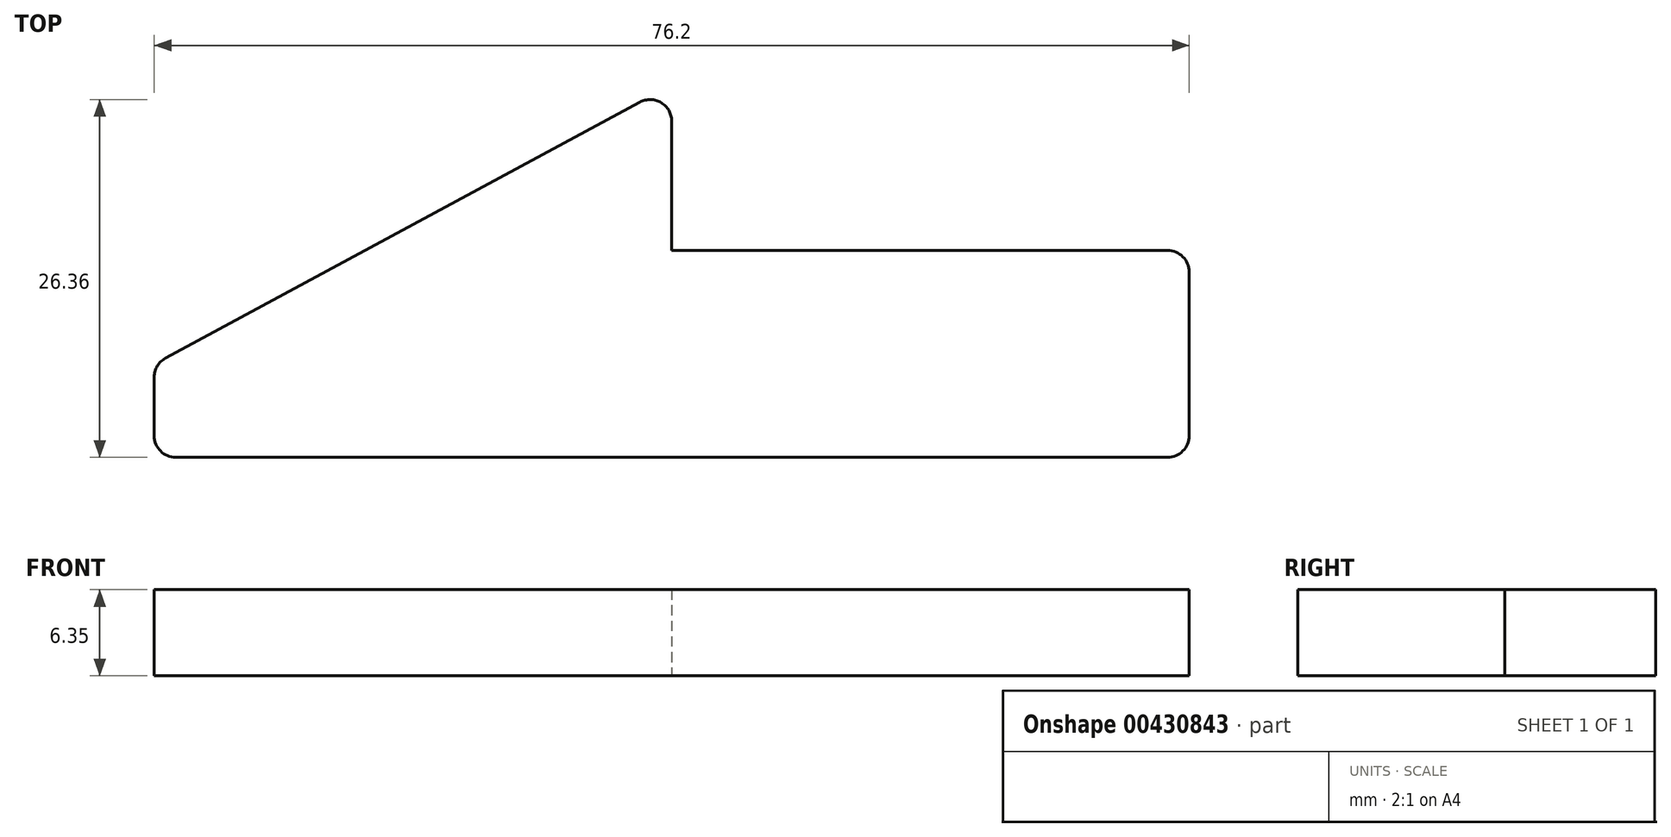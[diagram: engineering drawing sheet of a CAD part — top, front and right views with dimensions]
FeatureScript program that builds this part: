
annotation { "Feature Type Name" : "Feature", "Feature Type Description" : "" }
export const myFeature = defineFeature(function(context is Context, id is Id, definition is map)
    precondition{}
    {
        {
            var Q0;
            Q0=qCreatedBy(makeId("Top.planeOp"),FACE);
            var sketch = newSketch(context, id + "F0", { "sketchPlane" : qUnion([Q0])});
            skLineSegment(sketch, "E0", {"start": v(0, 0) * mm, "end": v(0, 6.86) * mm});
            skLineSegment(sketch, "E1", {"start": v(0, 6.86) * mm, "end": v(38.1, 27.43) * mm});
            skLineSegment(sketch, "E2", {"start": v(38.1, 27.43) * mm, "end": v(38.1, 15.24) * mm});
            skLineSegment(sketch, "E3", {"start": v(38.1, 15.24) * mm, "end": v(76.2, 15.24) * mm});
            skLineSegment(sketch, "E4", {"start": v(76.2, 15.24) * mm, "end": v(76.2, 0) * mm});
            skLineSegment(sketch, "E5", {"start": v(76.2, 0) * mm, "end": v(0, 0) * mm});
            skSolve(sketch);
        }
        {
            var Q0;
            Q0 = qSketchRegion(id + "F0", true);
            extrude(context, id + "F1", {"entities" : qUnion([Q0]), "depth" : 6.35 * mm});
        }
        {
            var Q0;
            Q0=makeQuery(id+"F1.opExtrude","SWEPT_EDGE",EDGE,{"disambiguationData":[OSD([sQuery(id+"F0.wireOp",EDGE,"E0"),sQuery(id+"F0.wireOp",EDGE,"E1")])]});
            var Q1;
            Q1=makeQuery(id+"F1.opExtrude","SWEPT_EDGE",EDGE,{"disambiguationData":[OSD([sQuery(id+"F0.wireOp",EDGE,"E1"),sQuery(id+"F0.wireOp",EDGE,"E2")])]});
            var Q2;
            Q2=makeQuery(id+"F1.opExtrude","SWEPT_EDGE",EDGE,{"disambiguationData":[OSD([sQuery(id+"F0.wireOp",EDGE,"E0"),sQuery(id+"F0.wireOp",EDGE,"E5")])]});
            var Q3;
            Q3=makeQuery(id+"F1.opExtrude","SWEPT_EDGE",EDGE,{"disambiguationData":[OSD([sQuery(id+"F0.wireOp",EDGE,"E3"),sQuery(id+"F0.wireOp",EDGE,"E4")])]});
            var Q4;
            Q4=makeQuery(id+"F1.opExtrude","SWEPT_EDGE",EDGE,{"disambiguationData":[OSD([sQuery(id+"F0.wireOp",EDGE,"E5"),sQuery(id+"F0.wireOp",EDGE,"E4")])]});
            fillet(context, id + "F2", {"entities" : qUnion([Q0, Q1, Q2, Q3, Q4]), "radius" : 1.59 * mm, "tangentPropagation" : true, "allowEdgeOverflow" : false});
        }
    });
